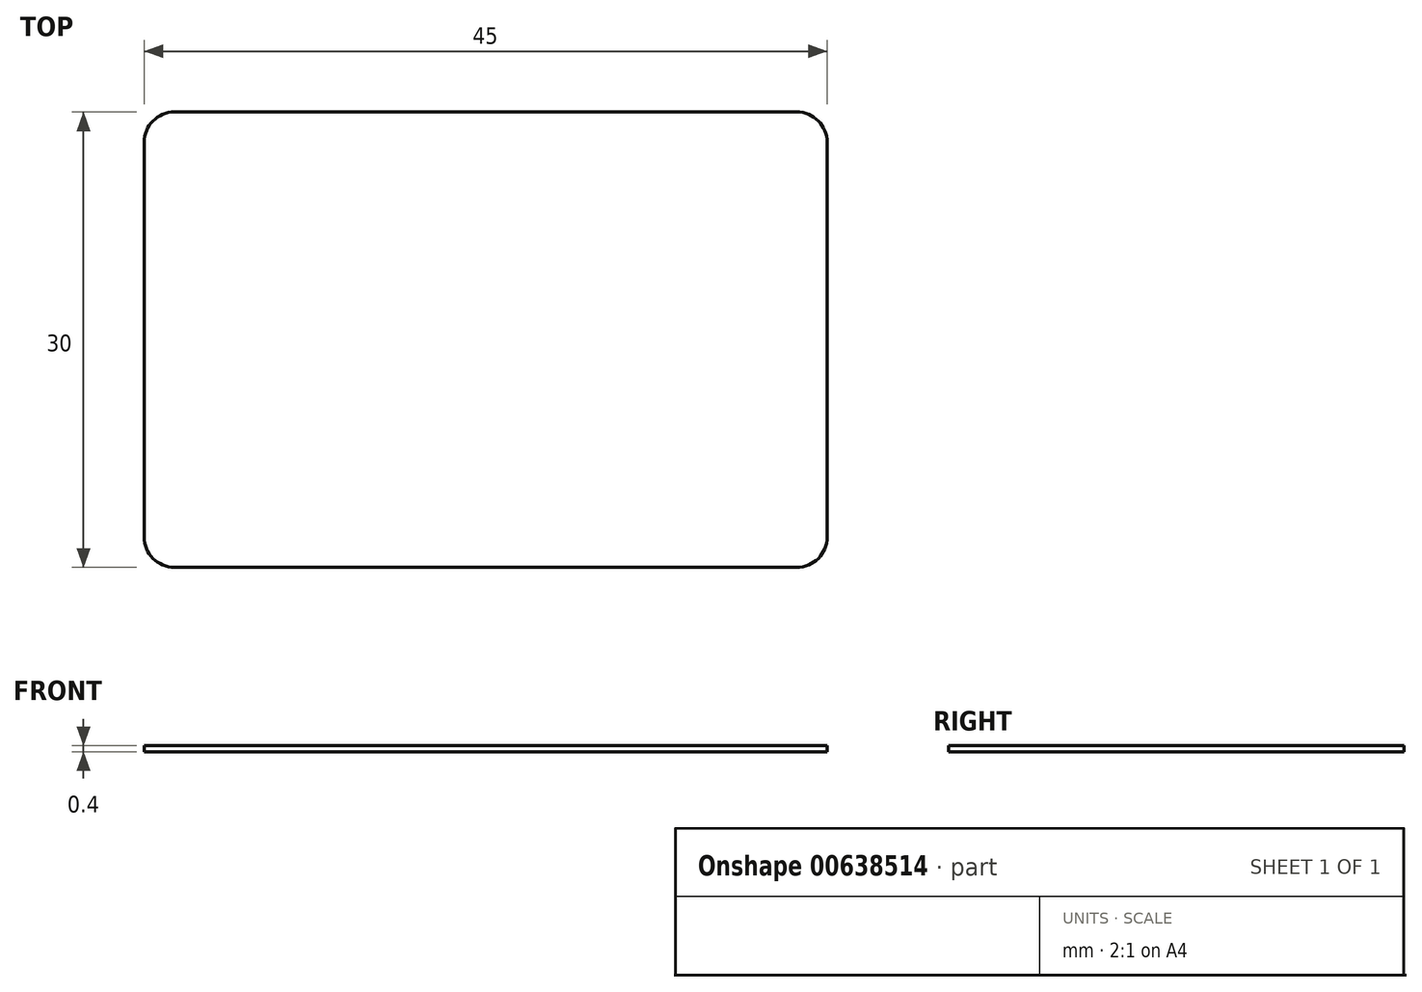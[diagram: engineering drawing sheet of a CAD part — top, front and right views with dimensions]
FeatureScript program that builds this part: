
annotation { "Feature Type Name" : "Feature", "Feature Type Description" : "" }
export const myFeature = defineFeature(function(context is Context, id is Id, definition is map)
    precondition{}
    {
        {
            var Q0;
            Q0=qCreatedBy(makeId("Top.planeOp"),FACE);
            var sketch = newSketch(context, id + "F0", { "sketchPlane" : qUnion([Q0])});
            skLineSegment(sketch, "E0.bottom", {"start": v(20.5, -15) * mm, "end": v(-20.5, -15) * mm});
            skLineSegment(sketch, "E0.top", {"start": v(20.5, 15) * mm, "end": v(-20.5, 15) * mm});
            skLineSegment(sketch, "E0.left", {"start": v(22.5, -13) * mm, "end": v(22.5, 13) * mm});
            skLineSegment(sketch, "E0.right", {"start": v(-22.5, -13) * mm, "end": v(-22.5, 13) * mm});
            skPoint(sketch, "E0.middle", {"position": v(0, 0) * mm});
            skPoint(sketch, "E1.visualSharp", {"position": v(-22.5, -15) * mm});
            skArc(sketch, "E1.filletArc", {"start": v(-22.5, -13) * mm, "mid": v(-21.91, -14.41) * mm, "end": v(-20.5, -15) * mm});
            skPoint(sketch, "E2.visualSharp", {"position": v(-22.5, 15) * mm});
            skArc(sketch, "E2.filletArc", {"start": v(-20.5, 15) * mm, "mid": v(-21.91, 14.41) * mm, "end": v(-22.5, 13) * mm});
            skPoint(sketch, "E3.visualSharp", {"position": v(22.5, -15) * mm});
            skArc(sketch, "E3.filletArc", {"start": v(20.5, -15) * mm, "mid": v(21.91, -14.41) * mm, "end": v(22.5, -13) * mm});
            skPoint(sketch, "E4.visualSharp", {"position": v(22.5, 15) * mm});
            skArc(sketch, "E4.filletArc", {"start": v(22.5, 13) * mm, "mid": v(21.91, 14.41) * mm, "end": v(20.5, 15) * mm});
            skSolve(sketch);
        }
        {
            var Q0;
            Q0=makeQuery(id+"F0.imprint","IMPRINT",FACE,{"disambiguationData":[TD([[makeQuery(id+"F0.imprint","IMPRINT",EDGE,{"derivedFrom":sQuery(id+"F0.wireOp",EDGE,"E0.bottom")}),-1.0]])]});
            extrude(context, id + "F1", {"entities" : qUnion([Q0]), "depth" : 0.4 * mm, "offsetDistance" : 25 * mm});
        }
    });
